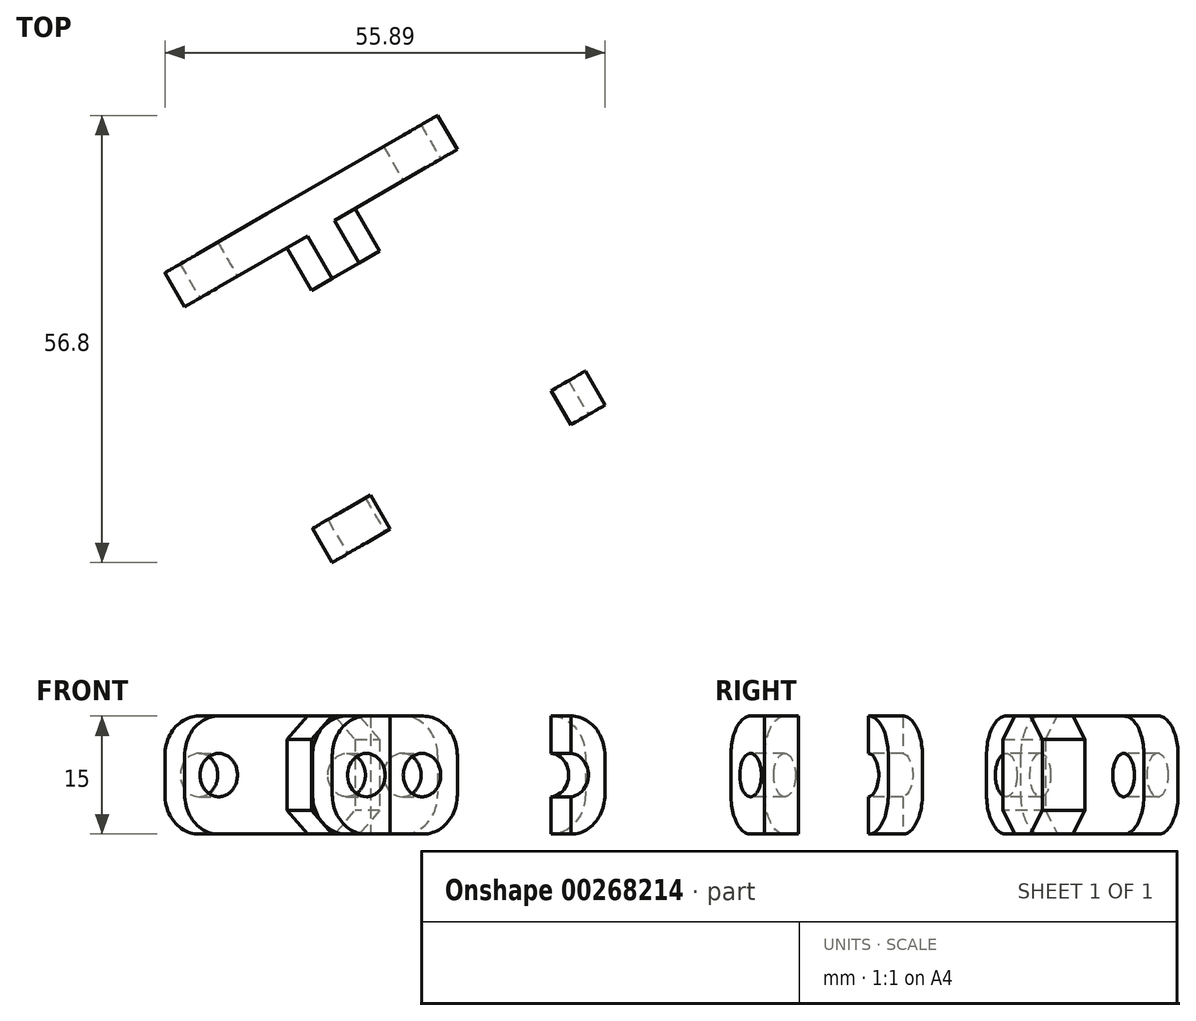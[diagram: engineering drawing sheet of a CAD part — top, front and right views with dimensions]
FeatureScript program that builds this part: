
annotation { "Feature Type Name" : "Feature", "Feature Type Description" : "" }
export const myFeature = defineFeature(function(context is Context, id is Id, definition is map)
    precondition{}
    {
        {
            var Q0;
            Q0=qCreatedBy(makeId("Top.planeOp"),FACE);
            var sketch = newSketch(context, id + "F0", { "sketchPlane" : qUnion([Q0])});
            skLineSegment(sketch, "E0", {"start": v(0, 0) * mm, "end": v(60, 0) * mm});
            skLineSegment(sketch, "E1", {"start": v(0, 0) * mm, "end": v(-60, 0) * mm});
            skLineSegment(sketch, "E2", {"start": v(-60, 0) * mm, "end": v(-90, 51.96) * mm});
            skLineSegment(sketch, "E3", {"start": v(-90, 51.96) * mm, "end": v(0, 103.92) * mm});
            skLineSegment(sketch, "E4", {"start": v(60, 0) * mm, "end": v(90, 51.96) * mm});
            skLineSegment(sketch, "E5", {"start": v(0, 103.92) * mm, "end": v(90, 51.96) * mm});
            skLineSegment(sketch, "E6", {"start": v(-87.8, 76.33) * mm, "end": v(-79.13, 81.33) * mm});
            skLineSegment(sketch, "E7", {"start": v(-68.8, 87.3) * mm, "end": v(-60.13, 92.3) * mm});
            skLineSegment(sketch, "E8", {"start": v(-100, 69.28) * mm, "end": v(-10, 121.24) * mm});
            skLineSegment(sketch, "E9", {"start": v(-100, 69.28) * mm, "end": v(-130, 121.24) * mm});
            skLineSegment(sketch, "E10", {"start": v(-130, 121.24) * mm, "end": v(-70, 225.17) * mm});
            skLineSegment(sketch, "E11", {"start": v(-70, 225.17) * mm, "end": v(-10, 225.17) * mm});
            skLineSegment(sketch, "E12", {"start": v(-10, 225.17) * mm, "end": v(-10, 121.24) * mm});
            skLineSegment(sketch, "E13", {"start": v(0, 0) * mm, "end": v(-52.5, 0) * mm});
            skLineSegment(sketch, "E14", {"start": v(-52.5, 0) * mm, "end": v(-78.75, 45.47) * mm});
            skLineSegment(sketch, "E15", {"start": v(0, 0) * mm, "end": v(52.5, 0) * mm});
            skLineSegment(sketch, "E16", {"start": v(52.5, 0) * mm, "end": v(78.75, 45.47) * mm});
            skLineSegment(sketch, "E17", {"start": v(78.75, 45.47) * mm, "end": v(0, 90.93) * mm});
            skLineSegment(sketch, "E18", {"start": v(0, 90.93) * mm, "end": v(-78.75, 45.47) * mm});
            skLineSegment(sketch, "E19", {"start": v(-100, 173.2) * mm, "end": v(-126.25, 127.74) * mm});
            skLineSegment(sketch, "E20", {"start": v(-100, 69.28) * mm, "end": v(-90, 51.96) * mm});
            skLineSegment(sketch, "E21", {"start": v(-126.25, 127.74) * mm, "end": v(-100, 82.27) * mm});
            skLineSegment(sketch, "E22", {"start": v(-100, 173.2) * mm, "end": v(-73.75, 218.67) * mm});
            skLineSegment(sketch, "E23", {"start": v(-73.75, 218.67) * mm, "end": v(-21.25, 218.67) * mm});
            skLineSegment(sketch, "E24", {"start": v(-21.25, 218.67) * mm, "end": v(-21.25, 127.74) * mm});
            skLineSegment(sketch, "E25", {"start": v(-21.25, 127.74) * mm, "end": v(-100, 82.27) * mm});
            skLineSegment(sketch, "E26", {"start": v(-100, 82.27) * mm, "end": v(-113, 74.77) * mm});
            skLineSegment(sketch, "E27", {"start": v(-113, 74.77) * mm, "end": v(-115.5, 79.1) * mm});
            skLineSegment(sketch, "E28", {"start": v(-115.5, 79.1) * mm, "end": v(-102.5, 86.6) * mm});
            skLineSegment(sketch, "E29", {"start": v(-78.75, 45.47) * mm, "end": v(-91.74, 37.97) * mm});
            skLineSegment(sketch, "E30", {"start": v(-91.74, 37.97) * mm, "end": v(-89.24, 33.64) * mm});
            skLineSegment(sketch, "E31", {"start": v(-89.24, 33.64) * mm, "end": v(-76.25, 41.14) * mm});
            skLineSegment(sketch, "E32", {"start": v(-91.74, 37.97) * mm, "end": v(-94.24, 42.3) * mm});
            skLineSegment(sketch, "E33", {"start": v(-94.24, 42.3) * mm, "end": v(-81.25, 49.8) * mm});
            skLineSegment(sketch, "E34", {"start": v(-113, 74.77) * mm, "end": v(-110.5, 70.44) * mm});
            skLineSegment(sketch, "E35", {"start": v(-110.5, 70.44) * mm, "end": v(-97.5, 77.94) * mm});
            skLineSegment(sketch, "E36", {"start": v(-97.5, 77.94) * mm, "end": v(-81.25, 49.8) * mm});
            skLineSegment(sketch, "E37", {"start": v(-78.75, 45.47) * mm, "end": v(-61.43, 55.47) * mm});
            skLineSegment(sketch, "E38", {"start": v(-61.43, 55.47) * mm, "end": v(-63.93, 59.8) * mm});
            skLineSegment(sketch, "E39", {"start": v(-63.93, 59.8) * mm, "end": v(-72.59, 54.8) * mm});
            skLineSegment(sketch, "E40", {"start": v(-72.59, 54.8) * mm, "end": v(-88.84, 82.94) * mm});
            skLineSegment(sketch, "E41", {"start": v(-88.84, 82.94) * mm, "end": v(-75.85, 90.44) * mm});
            skLineSegment(sketch, "E42", {"start": v(-75.85, 90.44) * mm, "end": v(-78.35, 94.77) * mm});
            skLineSegment(sketch, "E43", {"start": v(-63.93, 59.8) * mm, "end": v(-59.6, 62.3) * mm});
            skLineSegment(sketch, "E44", {"start": v(-59.6, 62.3) * mm, "end": v(-57.1, 57.97) * mm});
            skLineSegment(sketch, "E45", {"start": v(-57.1, 57.97) * mm, "end": v(-61.43, 55.47) * mm});
            skSolve(sketch);
        }
        {
            var Q0;
            {var subQ14=sQuery(id+"F0.wireOp",EDGE,"E41");Q0=makeQuery(id+"F0.imprint","IMPRINT",FACE,{"disambiguationData":[TD([[makeQuery(id+"F0.imprint","IMPRINT",EDGE,{"derivedFrom":subQ14}),1.0]])]});}
            var Q1;
            {var subQ5=sQuery(id+"F0.wireOp",EDGE,"E34");Q1=makeQuery(id+"F0.imprint","IMPRINT",FACE,{"disambiguationData":[TD([[makeQuery(id+"F0.imprint","IMPRINT",EDGE,{"derivedFrom":subQ5}),1.0]])]});}
            var Q2;
            {var subQ3=sQuery(id+"F0.wireOp",EDGE,"E8");var subQ7=makeQuery(id+"F0.imprint","IMPRINT",VERTEX,{"derivedFrom":subQ3});Q2=makeQuery(id+"F0.imprint","IMPRINT",FACE,{"disambiguationData":[TD([[makeQuery(id+"F0.imprint","IMPRINT",EDGE,{"disambiguationData":[TD([[subQ7,1.0]])],"derivedFrom":subQ3}),-1.0]])]});}
            var Q3;
            {var subQ0=sQuery(id+"F0.wireOp",EDGE,"E37");Q3=makeQuery(id+"F0.imprint","IMPRINT",FACE,{"disambiguationData":[TD([[makeQuery(id+"F0.imprint","IMPRINT",EDGE,{"derivedFrom":subQ0}),1.0]])]});}
            var Q4;
            {var subQ5=sQuery(id+"F0.wireOp",EDGE,"E32");Q4=makeQuery(id+"F0.imprint","IMPRINT",FACE,{"disambiguationData":[TD([[makeQuery(id+"F0.imprint","IMPRINT",EDGE,{"derivedFrom":subQ5}),-1.0]])]});}
            var Q5;
            Q5=makeQuery(id+"F0.imprint","IMPRINT",FACE,{"disambiguationData":[TD([[makeQuery(id+"F0.imprint","IMPRINT",EDGE,{"derivedFrom":sQuery(id+"F0.wireOp",EDGE,"E38")}),-1.0]])]});
            extrude(context, id + "F1", {"entities" : qUnion([Q0, Q1, Q2, Q3, Q4, Q5]), "depth" : 15 * mm});
        }
        {
            var Q0;
            Q0=makeQuery(id+"F1.opExtrude","SWEPT_FACE",FACE,{"disambiguationData":[OSD([sQuery(id+"F0.wireOp",EDGE,"E29"),sQuery(id+"F0.wireOp",EDGE,"E37")])]});
            var sketch = newSketch(context, id + "F2", { "sketchPlane" : qUnion([Q0])});
            skLineSegment(sketch, "E46", {"start": v(-60.47, 7.5) * mm, "end": v(-55.47, 7.5) * mm});
            skCircle(sketch, "E47", {"center": v(-55.47, 7.5) * mm, "radius": 2.75 * mm});
            skLineSegment(sketch, "E48", {"start": v(-55.47, 7.5) * mm, "end": v(-25.65, 7.5) * mm});
            skCircle(sketch, "E49", {"center": v(-25.65, 7.5) * mm, "radius": 2.75 * mm});
            skSolve(sketch);
        }
        {
            var Q0;
            {var subQ0=sQuery(id+"F2.wireOp",EDGE,"E48");var subQ1=sQuery(id+"F2.wireOp",EDGE,"E46");var subQ2=makeQuery(id+"F2.imprint","INTERSECT",VERTEX,{"derivedFrom":[subQ1,subQ0]});Q0=makeQuery(id+"F2.imprint","IMPRINT",FACE,{"disambiguationData":[TD([[makeQuery(id+"F2.imprint","IMPRINT",EDGE,{"disambiguationData":[TD([[subQ2,1.0]])],"derivedFrom":subQ1}),1.0]])]});}
            var Q1;
            {var subQ0=sQuery(id+"F2.wireOp",EDGE,"E48");var subQ1=sQuery(id+"F2.wireOp",EDGE,"E46");var subQ2=makeQuery(id+"F2.imprint","INTERSECT",VERTEX,{"derivedFrom":[subQ1,subQ0]});Q1=makeQuery(id+"F2.imprint","IMPRINT",FACE,{"disambiguationData":[TD([[makeQuery(id+"F2.imprint","IMPRINT",EDGE,{"disambiguationData":[TD([[subQ2,1.0]])],"derivedFrom":subQ1}),-1.0]])]});}
            var Q2;
            Q2=makeQuery(id+"F2.imprint","IMPRINT",FACE,{"disambiguationData":[TD([[makeQuery(id+"F2.imprint","IMPRINT",EDGE,{"derivedFrom":sQuery(id+"F2.wireOp",EDGE,"E49")}),1.0]])]});
            extrude(context, id + "F3", {"entities" : qUnion([Q0, Q1, Q2]), "operationType" : NewBodyOperationType.REMOVE, "oppositeDirection" : true, "depth" : 60 * mm});
        }
        {
            var Q0;
            Q0=makeQuery(id+"F1.opExtrude","CAP_EDGE",EDGE,{"disambiguationData":[OSD([sQuery(id+"F0.wireOp",EDGE,"E36")])],"isStart":false});
            var Q1;
            Q1=makeQuery(id+"F1.opExtrude","CAP_EDGE",EDGE,{"disambiguationData":[OSD([sQuery(id+"F0.wireOp",EDGE,"E40")])],"isStart":false});
            var Q2;
            Q2=makeQuery(id+"F1.opExtrude","CAP_EDGE",EDGE,{"disambiguationData":[OSD([sQuery(id+"F0.wireOp",EDGE,"E36")])],"isStart":true});
            var Q3;
            Q3=makeQuery(id+"F1.opExtrude","CAP_EDGE",EDGE,{"disambiguationData":[OSD([sQuery(id+"F0.wireOp",EDGE,"E40")])],"isStart":true});
            chamfer(context, id + "F4", {"entities" : qUnion([Q0, Q1, Q2, Q3]), "width" : 3 * mm, "tangentPropagation" : true});
        }
        {
            var Q0;
            Q0=makeQuery(id+"F1.opExtrude","CAP_EDGE",EDGE,{"disambiguationData":[OSD([sQuery(id+"F0.wireOp",EDGE,"E32")])],"isStart":true});
            var Q1;
            Q1=makeQuery(id+"F1.opExtrude","CAP_EDGE",EDGE,{"disambiguationData":[OSD([sQuery(id+"F0.wireOp",EDGE,"E34")])],"isStart":true});
            var Q2;
            Q2=makeQuery(id+"F1.opExtrude","CAP_EDGE",EDGE,{"disambiguationData":[OSD([sQuery(id+"F0.wireOp",EDGE,"E34")])],"isStart":false});
            var Q3;
            Q3=makeQuery(id+"F1.opExtrude","CAP_EDGE",EDGE,{"disambiguationData":[OSD([sQuery(id+"F0.wireOp",EDGE,"E32")])],"isStart":false});
            var Q4;
            Q4=makeQuery(id+"F1.opExtrude","CAP_EDGE",EDGE,{"disambiguationData":[OSD([sQuery(id+"F0.wireOp",EDGE,"E44")])],"isStart":false});
            var Q5;
            Q5=makeQuery(id+"F1.opExtrude","CAP_EDGE",EDGE,{"disambiguationData":[OSD([sQuery(id+"F0.wireOp",EDGE,"E44")])],"isStart":true});
            var Q6;
            Q6=makeQuery(id+"F1.opExtrude","CAP_EDGE",EDGE,{"disambiguationData":[OSD([sQuery(id+"F0.wireOp",EDGE,"E42")])],"isStart":false});
            var Q7;
            Q7=makeQuery(id+"F1.opExtrude","CAP_EDGE",EDGE,{"disambiguationData":[OSD([sQuery(id+"F0.wireOp",EDGE,"E42")])],"isStart":true});
            fillet(context, id + "F5", {"entities" : qUnion([Q0, Q1, Q2, Q3, Q4, Q5, Q6, Q7]), "radius" : 5 * mm, "tangentPropagation" : true, "allowEdgeOverflow" : false});
        }
    });
